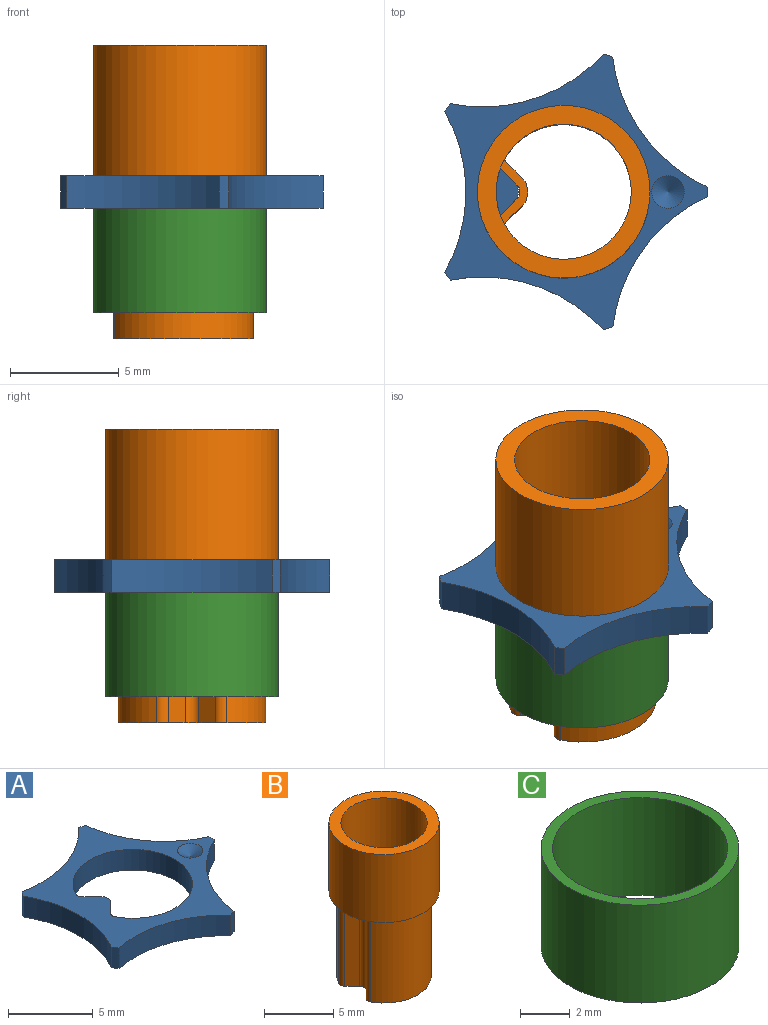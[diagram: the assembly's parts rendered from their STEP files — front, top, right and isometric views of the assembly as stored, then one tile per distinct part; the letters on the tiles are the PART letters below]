
ASSEMBLY  parts=3 mates=2
PART A: 19 faces, bbox 12.1x12.7x1.5 mm
  f0: cylinder r=7.5mm len=7.03mm, axis (0,0,-1), area 11.6mm2, adj f1,f15,f16,f17
  f1: cylinder r=6.6mm len=1.5mm, axis (0,0,-1), area 0.7mm2, adj f0,f2,f16,f17
  f2: cylinder r=7.5mm len=7.39mm, axis (0,0,-1), area 11.6mm2, adj f1,f3,f16,f17
  f3: cylinder r=6.6mm len=1.5mm, axis (0,0,-1), area 0.7mm2, adj f2,f4,f16,f17
  f4: cylinder r=7.5mm len=7.02mm, axis (0,0,-1), area 11.6mm2, adj f3,f5,f16,f17
  f5: cylinder r=6.6mm len=1.5mm, axis (0,0,-1), area 0.7mm2, adj f4,f6,f16,f17
  f6: cylinder r=7.5mm len=5.97mm, axis (0,0,-1), area 11.6mm2, adj f5,f7,f16,f17
  f7: cylinder r=6.6mm len=1.5mm, axis (0,0,-1), area 0.7mm2, adj f6,f8,f16,f17
  f8: cylinder r=7.5mm len=5.98mm, axis (0,0,-1), area 11.6mm2, adj f7,f15,f16,f17
  f9: cylinder r=3.53mm len=7.06mm, axis (0,0,-1), area 28.3mm2, adj f10,f14,f16,f17
  f10: cylinder r=0.3mm len=1.5mm, axis (0,0,-1), area 0.6mm2, adj f9,f11,f16,f17
  f11: plane 1.5x0.83mm, normal (0.71,-0.71,0), area 1.8mm2, adj f10,f12,f16,f17
  f12: cylinder r=0.6mm len=1.5mm, axis (0,0,-1), area 1.4mm2, adj f11,f13,f16,f17
  f13: plane 1.5x0.83mm, normal (0.71,0.71,0), area 1.8mm2, adj f12,f14,f16,f17
  f14: cylinder r=0.3mm len=1.5mm, axis (0,0,-1), area 0.6mm2, adj f9,f13,f16,f17
  f15: cylinder r=6.6mm len=1.5mm, axis (0,0,-1), area 0.7mm2, adj f0,f8,f16,f17
  f16: plane 12.69x12.07mm, normal (0,0,1), area 45.8mm2, adj f0,f1,f2,f3,f4,f5,f6,f7
  f17: plane 12.69x12.07mm, normal (0,0,-1), area 47.6mm2, adj f0,f1,f2,f3,f4,f5,f6,f7
  f18: cone r=0.75mm half-angle=60deg, axis (0,0,1), area 2mm2, adj f16
PART B: 17 faces, bbox 7.9x7.9x13.5 mm
  f0: cylinder r=3.11mm len=13.5mm, axis (0,0,-1), area 239mm2, adj f2,f3,f4,f14,f15,f16
  f1: cylinder r=3.97mm len=7.94mm, axis (0,0,-1), area 149.7mm2, adj f2,f3
  f2: plane 7.94x7.94mm, normal (0,0,1), area 19.2mm2, adj f0,f1
  f3: plane 7.94x7.94mm, normal (0,0,-1), area 14mm2, adj f0,f1,f9,f10,f11
  f4: cylinder r=0.15mm len=7.5mm, axis (0,0,1), area 1.5mm2, adj f0,f5,f15,f16
  f5: plane 7.5x0.75mm, normal (0.71,0.71,0), area 7.9mm2, adj f4,f6,f15,f16
  f6: cylinder r=0.9mm len=7.5mm, axis (0,0,1), area 10.6mm2, adj f5,f7,f15,f16
  f7: plane 7.5x0.75mm, normal (0.71,-0.71,0), area 7.9mm2, adj f6,f14,f15,f16
  f8: plane 7.5x0.76mm, normal (-0.71,-0.71,0), area 8.1mm2, adj f9,f13,f15,f16
  f9: cylinder r=0.45mm len=7.5mm, axis (0,0,1), area 4.3mm2, adj f3,f8,f10,f15,f16
  f10: cylinder r=3.4mm len=7.5mm, axis (0,0,1), area 134.8mm2, adj f3,f9,f11,f15
  f11: cylinder r=0.45mm len=7.5mm, axis (0,0,1), area 4.3mm2, adj f3,f10,f12,f15,f16
  f12: plane 7.5x0.76mm, normal (-0.71,0.71,0), area 8.1mm2, adj f11,f13,f15,f16
  f13: cylinder r=0.45mm len=7.5mm, axis (0,0,1), area 5.3mm2, adj f8,f12,f15,f16
  f14: cylinder r=0.15mm len=7.5mm, axis (0,0,1), area 1.5mm2, adj f0,f7,f15,f16
  f15: plane 6.79x6.44mm, normal (0,0,-1), area 6.4mm2, adj f0,f4,f5,f6,f7,f8,f9,f10
  f16: plane 3.13x1.26mm, normal (0,0,1), area 1.3mm2, adj f0,f4,f5,f6,f7,f8,f9,f11
PART C: 4 faces, bbox 7.9x7.9x4.8 mm
  f0: cylinder r=3.51mm len=7.02mm, axis (0,0,-1), area 105.8mm2, adj f2,f3
  f1: cylinder r=3.97mm len=7.94mm, axis (0,0,-1), area 119.7mm2, adj f2,f3
  f2: plane 7.94x7.94mm, normal (0,0,1), area 10.8mm2, adj f0,f1
  f3: plane 7.94x7.94mm, normal (0,0,-1), area 10.8mm2, adj f0,f1
PLACE A t=(0,0,-1.5)mm
PLACE B at identity fixed
PLACE C t=(0,0,-6.3)mm
MATE fastened B.f0 <-> A.f1  axis (0,0,1) through (0,0,0)mm
MATE fastened A.f1 <-> C.f0  axis (0,0,1) through (0,0,-1.5)mm
